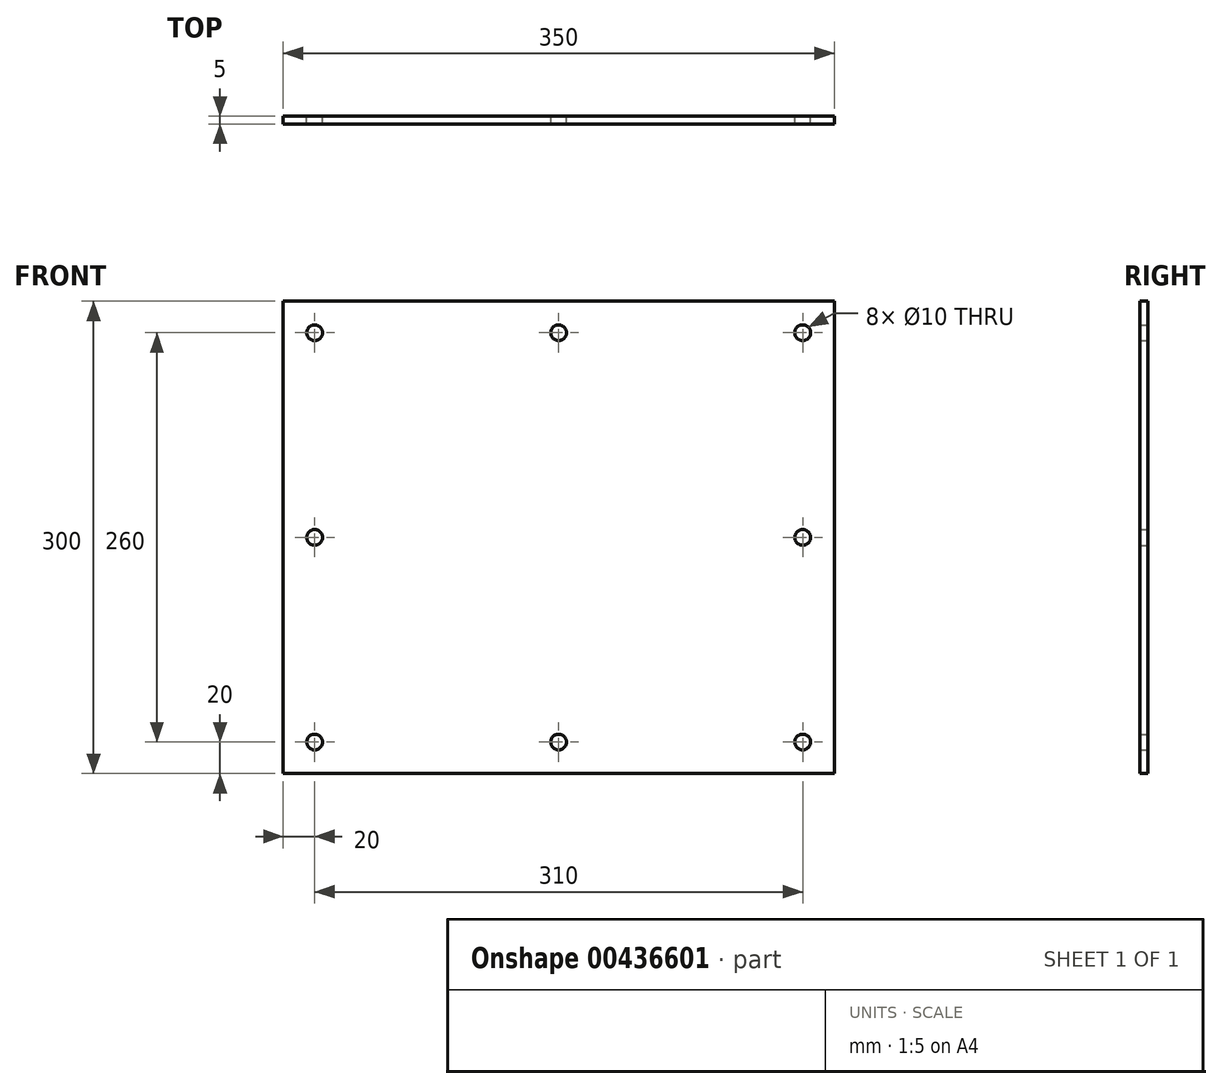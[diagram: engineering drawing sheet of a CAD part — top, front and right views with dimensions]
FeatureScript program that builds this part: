
annotation { "Feature Type Name" : "Feature", "Feature Type Description" : "" }
export const myFeature = defineFeature(function(context is Context, id is Id, definition is map)
    precondition{}
    {
        {
            var Q0;
            Q0=qCreatedBy(makeId("Front.planeOp"),FACE);
            var sketch = newSketch(context, id + "F0", { "sketchPlane" : qUnion([Q0])});
            skLineSegment(sketch, "E0.bottom", {"start": v(175, -150) * mm, "end": v(-175, -150) * mm});
            skLineSegment(sketch, "E0.top", {"start": v(175, 150) * mm, "end": v(-175, 150) * mm});
            skLineSegment(sketch, "E0.left", {"start": v(175, -150) * mm, "end": v(175, 150) * mm});
            skLineSegment(sketch, "E0.right", {"start": v(-175, -150) * mm, "end": v(-175, 150) * mm});
            skPoint(sketch, "E0.middle", {"position": v(0, 0) * mm});
            skCircle(sketch, "E1", {"center": v(-155, 130) * mm, "radius": 5 * mm});
            skCircle(sketch, "E2", {"center": v(-155, -130) * mm, "radius": 5 * mm});
            skCircle(sketch, "E3", {"center": v(155, 130) * mm, "radius": 5 * mm});
            skCircle(sketch, "E4", {"center": v(155, -130) * mm, "radius": 5 * mm});
            skCircle(sketch, "E5", {"center": v(0, 130) * mm, "radius": 5 * mm});
            skCircle(sketch, "E6", {"center": v(0, -130) * mm, "radius": 5 * mm});
            skCircle(sketch, "E7", {"center": v(-155, 0) * mm, "radius": 5 * mm});
            skCircle(sketch, "E8", {"center": v(155, 0) * mm, "radius": 5 * mm});
            skSolve(sketch);
        }
        {
            var Q0;
            Q0 = qSketchRegion(id + "F0", true);
            extrude(context, id + "F1", {"entities" : qUnion([Q0]), "depth" : 5 * mm});
        }
    });
